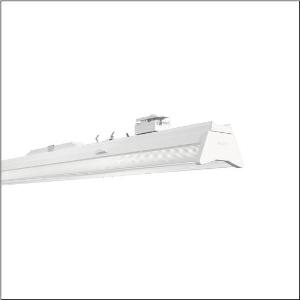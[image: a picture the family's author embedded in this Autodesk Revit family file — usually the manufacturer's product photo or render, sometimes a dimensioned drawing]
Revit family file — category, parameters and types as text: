
# Revit family: licross_r__21_performance_mo_51td16vn465g_a773
name_source: partatom
category: Lighting Fixtures
units: mm (PartAtom-declared; Revit-internal decimal feet)

## family parameters
Cut with Voids When Loaded = No
Host = Face
Light Source = No
Part Type = Normal
Room Calculation Point = No
Round Connector Dimension = Use Diameter
Shared = No

## types (1)
- --- (1 x LED, 6500 lm, 34.9 W, 4000K)
    Apparent Load = 35 VA
    CIE Flux Codes = 66 88 96 79 100
    Color Rendering = 80
    Color Temperature = 4000K
    Default Elevation = 1800 mm
    Description = Licross® 21 Performance MO, luminaire insert, of sheet steel, galvanised, coil coated, white, length: 1.500mm, width: 120mm, height: 123mm, LED rated luminous flux: 6.500lm, light colour: 840, SDCM (Standard Deviation of Colour Matching)MacAdam ≤ 2 SDCM (initial), control gear: DALI 2, CLO, with plug, 5-pole, with phase selection, mains connection: 220..240V, AC, 50/60Hz, start of lifetime: 35W, end of service life: 38W, internal wiring halogen-free, primary light control with lens, of plastic, primary optical cover: cover, of PMMA, light emission: direct/indirect distribution, primary light characteristic: symmetric, protection rating (complete): IP54, insulation class (complete): insulation class I (protective earthing), certification: CE, ENEC, VDE, UKCA, protection symbol: D if used in an environment with non-conductive dust loads with corresponding accessories, impact resistance: IK06, permissible ambient temperature for indoor applications: -25..+40°C, corresponds to IFS (International Featured Standards) requirements for safety and quality in the food industry, reducing of maximum allowable ambient temperature of 5°C with ceiling mounting, LABS conformity tested according to VDMA 24364:2018-05, packaging unit: 1 piece
    Height = 114 mm
    Lamp = 1 x LED
    Lamp Light Flux = 6500 lm
    Lamp Power = 34.9 W
    Lamp count = 1
    Length = 1500 mm
    Luminous efficacy = 186 lm/W
    Manufacturer = Siteco
    ModVariant = No
    Model = 51TD16VN465G
    Mounting Place = Ceiling
    Mounting Type = Pendant
    Number of Poles = 1
    OnlyDefault = Yes
    Power Factor = 1
    Product Name = Licross® 21 Performance MO
    Product group = luminaire insert | ceiling pendant
    ProductGroupID = 901
    Protection Class = Protection class I
    Protection Degree = IP 54
    RLX_Detail_Level = 1
    RLX_Emergency_Light_Flux = 0 lm
    RLX_Emergency_Type = 0
    RLX_Emergency_Type_DB = No
    RlxData = <blob elided: 34089 chars, md5=d2c590f0>
    Socket = socket
    Standby Power = 0 W
    System Light Flux = 6500 lm
    System Power = 35 W
    Type Comments = factory setting: luminous flux: 100 % | dim-lin: 254 | 236 mA
    Type Image = l_1256138.jpg
    URL = http://relux.com
    VarID = @adj_095581
    Voltage = 0 V
    Weight = 0.00 kg
    Width = 120 mm

## geometry (parser evidence)
native form markers: Blend x4, Sweep x12
no freeform markers — native parametric forms only
